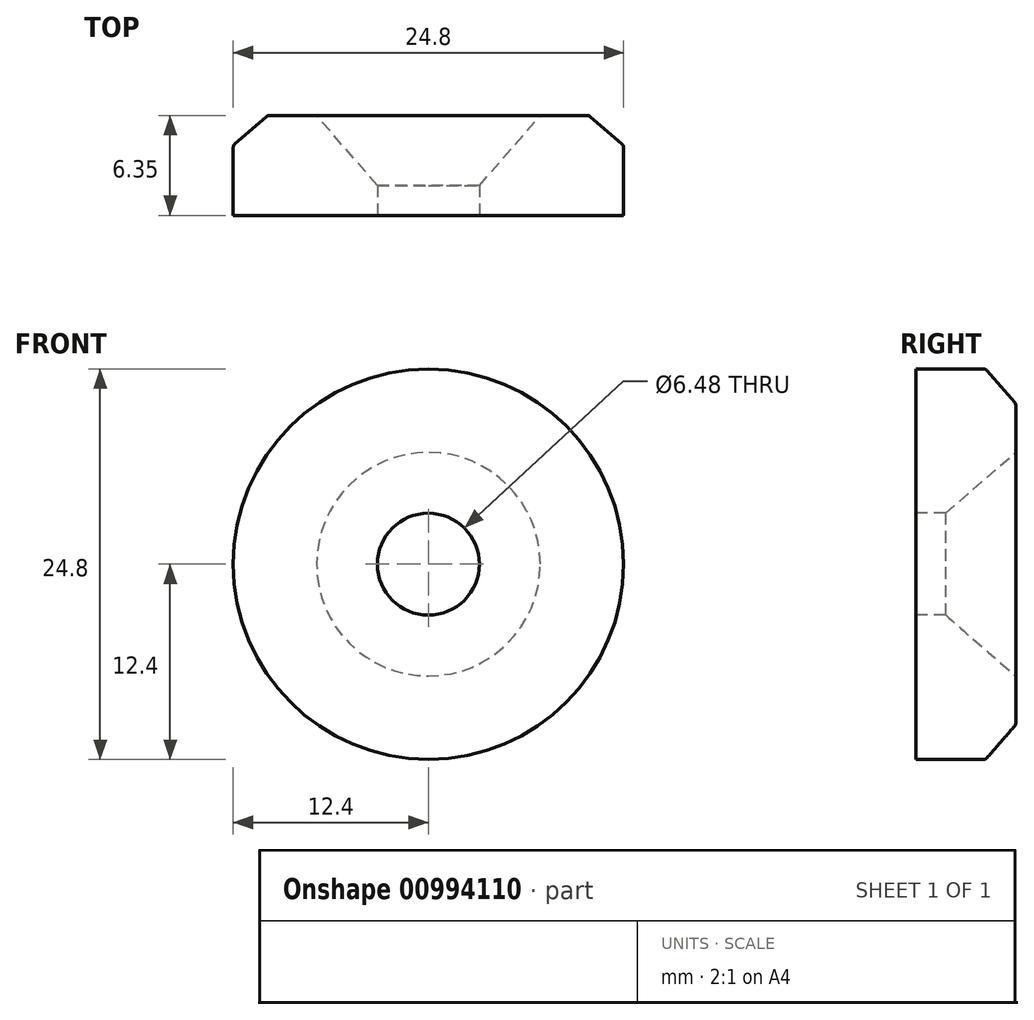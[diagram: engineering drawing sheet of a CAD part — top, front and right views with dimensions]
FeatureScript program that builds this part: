
annotation { "Feature Type Name" : "Feature", "Feature Type Description" : "" }
export const myFeature = defineFeature(function(context is Context, id is Id, definition is map)
    precondition{}
    {
        {
            var Q0;
            Q0=qCreatedBy(makeId("Top.planeOp"),FACE);
            var sketch = newSketch(context, id + "F0", { "sketchPlane" : qUnion([Q0])});
            skLineSegment(sketch, "E0", {"start": v(0, 0) * mm, "end": v(-12.4, 0) * mm});
            skLineSegment(sketch, "E1", {"start": v(-12.4, 0) * mm, "end": v(-12.4, 4.45) * mm});
            skLineSegment(sketch, "E2", {"start": v(-12.4, 4.45) * mm, "end": v(-10.2, 6.35) * mm});
            skLineSegment(sketch, "E3.0", {"start": v(-3.24, 0) * mm, "end": v(-3.24, 1.9) * mm});
            skLineSegment(sketch, "E4", {"start": v(-3.24, 1.9) * mm, "end": v(-7.1, 6.35) * mm});
            skLineSegment(sketch, "E5.trimOffspring", {"start": v(-7.1, 6.35) * mm, "end": v(-10.2, 6.35) * mm});
            skLineSegment(sketch, "E6", {"start": v(0, 0) * mm, "end": v(0, 9.34) * mm, "construction": true});
            skSolve(sketch);
        }
        {
            var Q0;
            {var subQ1=sQuery(id+"F0.wireOp",EDGE,"E1");Q0=makeQuery(id+"F0.imprint","IMPRINT",FACE,{"disambiguationData":[TD([[makeQuery(id+"F0.imprint","IMPRINT",EDGE,{"derivedFrom":subQ1}),-1.0]])]});}
            var Q1;
            Q1=sQuery(id+"F0.wireOp",EDGE,"E6");
            var Q2;
            Q2=sQuery(id+"F0.wireOp",EDGE,"E6");
            revolve(context, id + "F1", {"surfaceOperationType" : NewSurfaceOperationType.NEW, "entities" : qUnion([Q0]), "surfaceEntities" : qUnion([Q1]), "axis" : qUnion([Q2]), "revolveType" : RevolveType.FULL});
        }
        {
            var Q0;
            Q0=makeQuery(id+"F1.opRevolve","SWEPT_EDGE",EDGE,{"disambiguationData":[OSD([sQuery(id+"F0.wireOp",EDGE,"E1"),sQuery(id+"F0.wireOp",EDGE,"E2")])]});
            var Q1;
            Q1=makeQuery(id+"F1.opRevolve","SWEPT_EDGE",EDGE,{"disambiguationData":[OSD([sQuery(id+"F0.wireOp",EDGE,"E2"),sQuery(id+"F0.wireOp",EDGE,"E5.trimOffspring")])]});
            fillet(context, id + "F2", {"entities" : qUnion([Q0, Q1]), "radius" : 0.25 * mm, "tangentPropagation" : true, "allowEdgeOverflow" : false});
        }
    });
